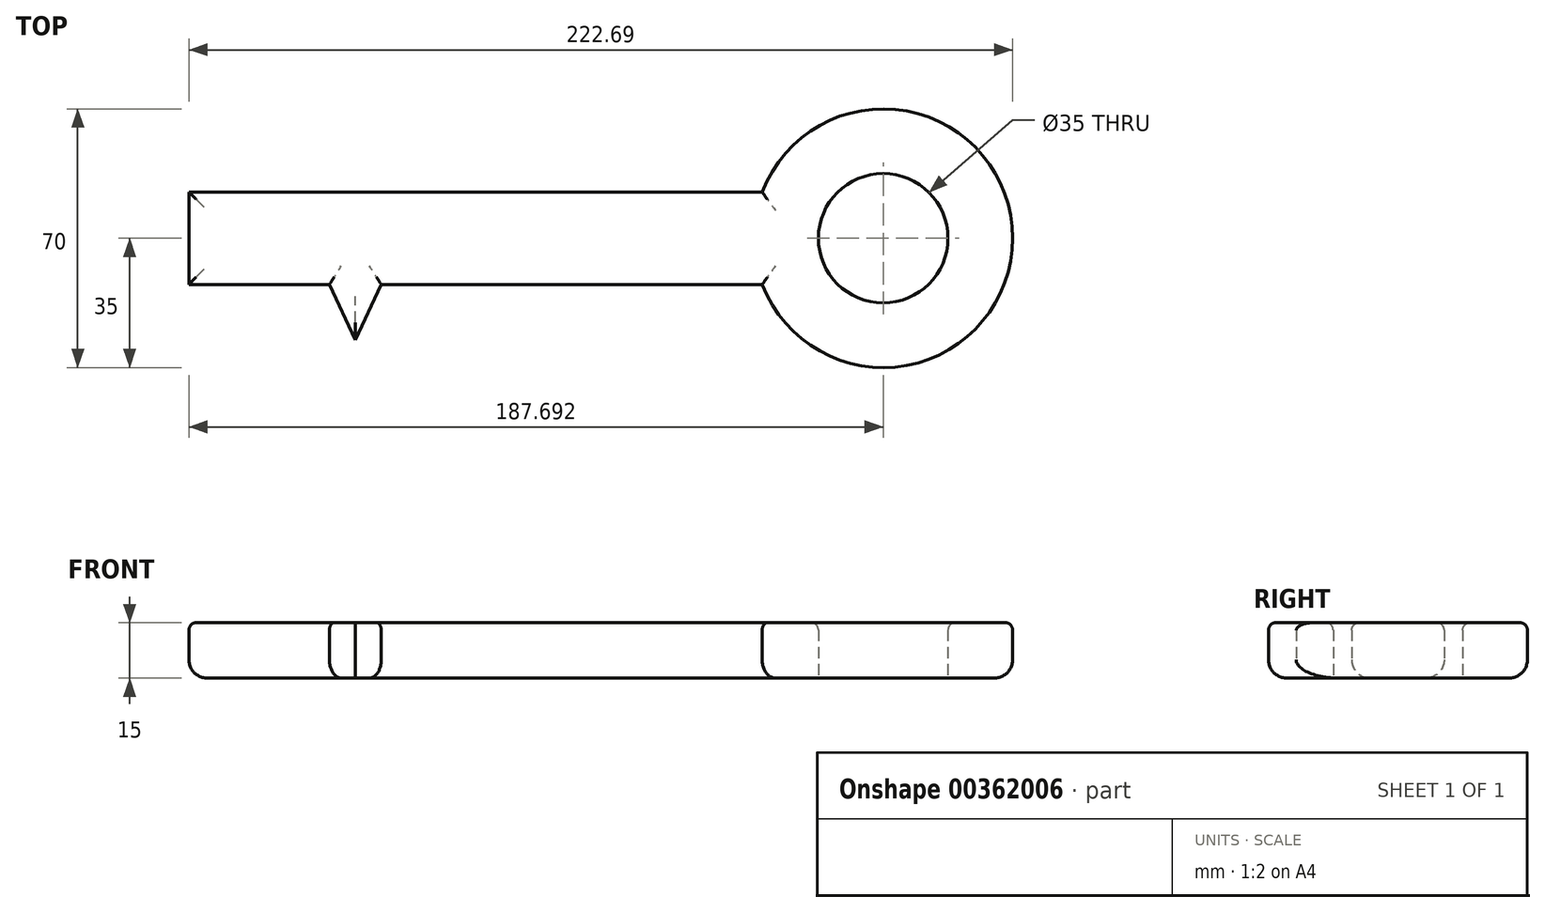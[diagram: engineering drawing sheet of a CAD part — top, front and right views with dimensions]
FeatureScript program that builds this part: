
annotation { "Feature Type Name" : "Feature", "Feature Type Description" : "" }
export const myFeature = defineFeature(function(context is Context, id is Id, definition is map)
    precondition{}
    {
        {
            var Q0;
            Q0=qCreatedBy(makeId("Top.planeOp"),FACE);
            var sketch = newSketch(context, id + "F0", { "sketchPlane" : qUnion([Q0])});
            skLineSegment(sketch, "E0.bottom", {"start": v(-155, 12.5) * mm, "end": v(0, 12.5) * mm});
            skLineSegment(sketch, "E0.top", {"start": v(-155, -12.5) * mm, "end": v(0, -12.5) * mm});
            skLineSegment(sketch, "E0.left", {"start": v(-155, 12.5) * mm, "end": v(-155, -12.5) * mm});
            skLineSegment(sketch, "E0.right", {"start": v(0, 12.5) * mm, "end": v(0, -12.5) * mm});
            skLineSegment(sketch, "E1.bottom", {"start": v(0, -12.5) * mm, "end": v(-155, -12.5) * mm});
            skLineSegment(sketch, "E1.top", {"start": v(0, -12.5) * mm, "end": v(-155, -12.5) * mm});
            skLineSegment(sketch, "E1.left", {"start": v(0, -12.5) * mm, "end": v(0, -12.5) * mm});
            skLineSegment(sketch, "E1.right", {"start": v(-155, -12.5) * mm, "end": v(-155, -12.5) * mm});
            skLineSegment(sketch, "E2.bottom", {"start": v(-155, -12.5) * mm, "end": v(-145, -12.5) * mm});
            skLineSegment(sketch, "E2.top", {"start": v(-155, -42.5) * mm, "end": v(-145, -42.5) * mm});
            skLineSegment(sketch, "E2.left", {"start": v(-155, -12.5) * mm, "end": v(-155, -42.5) * mm});
            skLineSegment(sketch, "E2.right", {"start": v(-145, -12.5) * mm, "end": v(-145, -42.5) * mm});
            skLineSegment(sketch, "E3.bottom", {"start": v(-135, -12.5) * mm, "end": v(-127, -12.5) * mm});
            skLineSegment(sketch, "E3.top", {"start": v(-135, -27.5) * mm, "end": v(-127, -27.5) * mm});
            skLineSegment(sketch, "E3.left", {"start": v(-135, -12.5) * mm, "end": v(-135, -27.5) * mm});
            skLineSegment(sketch, "E3.right", {"start": v(-127, -12.5) * mm, "end": v(-127, -27.5) * mm});
            skLineSegment(sketch, "E4", {"start": v(-117, -12.5) * mm, "end": v(-110, -27.5) * mm});
            skLineSegment(sketch, "E5", {"start": v(-110, -27.5) * mm, "end": v(-103, -12.5) * mm});
            skCircle(sketch, "E6", {"center": v(32.7, 0) * mm, "radius": 17.5 * mm});
            skArc(sketch, "E7", {"start": v(0, -12.5) * mm, "mid": v(67.7, 0) * mm, "end": v(0, 12.5) * mm});
            skSolve(sketch);
        }
        {
            var Q0;
            Q0=makeQuery(id+"F0.imprint","IMPRINT",FACE,{"disambiguationData":[TD([[makeQuery(id+"F0.imprint","IMPRINT",EDGE,{"derivedFrom":sQuery(id+"F0.wireOp",EDGE,"E2.bottom")}),-1.0]])]});
            var Q1;
            Q1=makeQuery(id+"F0.imprint","IMPRINT",FACE,{"disambiguationData":[TD([[makeQuery(id+"F0.imprint","IMPRINT",EDGE,{"derivedFrom":sQuery(id+"F0.wireOp",EDGE,"E3.bottom")}),-1.0]])]});
            var Q2;
            {var subQ0=sQuery(id+"F0.wireOp",EDGE,"E4");Q2=makeQuery(id+"F0.imprint","IMPRINT",FACE,{"disambiguationData":[TD([[makeQuery(id+"F0.imprint","IMPRINT",EDGE,{"derivedFrom":subQ0}),1.0]])]});}
            var Q3;
            Q3=makeQuery(id+"F0.imprint","IMPRINT",FACE,{"disambiguationData":[TD([[makeQuery(id+"F0.imprint","IMPRINT",EDGE,{"derivedFrom":sQuery(id+"F0.wireOp",EDGE,"E0.bottom")}),-1.0]])]});
            var Q4;
            Q4=makeQuery(id+"F0.imprint","IMPRINT",FACE,{"disambiguationData":[TD([[makeQuery(id+"F0.imprint","IMPRINT",EDGE,{"derivedFrom":sQuery(id+"F0.wireOp",EDGE,"E0.right")}),1.0]])]});
            extrude(context, id + "F1", {"entities" : qUnion([Q0, Q1, Q2, Q3, Q4]), "depth" : 15 * mm});
        }
        {
            var Q0;
            Q0=makeQuery(id+"F1.opExtrude","CAP_EDGE",EDGE,{"disambiguationData":[OSD([sQuery(id+"F0.wireOp",EDGE,"E7")])],"isStart":false});
            var Q1;
            Q1=makeQuery(id+"F1.opExtrude","CAP_EDGE",EDGE,{"disambiguationData":[OSD([sQuery(id+"F0.wireOp",EDGE,"E6")])],"isStart":false});
            var Q2;
            {var subQ0=sQuery(id+"F0.wireOp",EDGE,"E0.top");Q2=makeQuery(id+"F1.opExtrude","CAP_EDGE",EDGE,{"disambiguationData":[OSD([subQ0]),TDD([makeQuery(id+"F0.imprint","IMPRINT",EDGE,{"disambiguationData":[TD([[makeQuery(id+"F0.imprint","INTERSECT",VERTEX,{"derivedFrom":[subQ0,sQuery(id+"F0.wireOp",EDGE,"E5")]}),-1.0]])],"derivedFrom":subQ0})])],"isStart":false});}
            var Q3;
            Q3=makeQuery(id+"F1.opExtrude","CAP_EDGE",EDGE,{"disambiguationData":[OSD([sQuery(id+"F0.wireOp",EDGE,"E0.bottom")])],"isStart":false});
            var Q4;
            Q4=makeQuery(id+"F1.opExtrude","CAP_EDGE",EDGE,{"disambiguationData":[OSD([sQuery(id+"F0.wireOp",EDGE,"E5")])],"isStart":false});
            var Q5;
            Q5=makeQuery(id+"F1.opExtrude","CAP_EDGE",EDGE,{"disambiguationData":[OSD([sQuery(id+"F0.wireOp",EDGE,"E4")])],"isStart":false});
            var Q6;
            Q6=makeQuery(id+"F1.opExtrude","CAP_EDGE",EDGE,{"disambiguationData":[OSD([sQuery(id+"F0.wireOp",EDGE,"E3.top")])],"isStart":false});
            var Q7;
            Q7=makeQuery(id+"F1.opExtrude","CAP_FACE",FACE,{"disambiguationData":[OSD([sQuery(id+"F0.wireOp",EDGE,"E0.bottom"),sQuery(id+"F0.wireOp",EDGE,"E0.left"),sQuery(id+"F0.wireOp",EDGE,"E0.top"),sQuery(id+"F0.wireOp",EDGE,"E2.top"),sQuery(id+"F0.wireOp",EDGE,"E2.left"),sQuery(id+"F0.wireOp",EDGE,"E2.right"),sQuery(id+"F0.wireOp",EDGE,"E3.top"),sQuery(id+"F0.wireOp",EDGE,"E3.left"),sQuery(id+"F0.wireOp",EDGE,"E3.right"),sQuery(id+"F0.wireOp",EDGE,"E4"),sQuery(id+"F0.wireOp",EDGE,"E5"),sQuery(id+"F0.wireOp",EDGE,"E6"),sQuery(id+"F0.wireOp",EDGE,"E7")])],"isStart":false});
            fillet(context, id + "F2", {"entities" : qUnion([Q0, Q1, Q2, Q3, Q4, Q5, Q6, Q7]), "radius" : 2 * mm, "tangentPropagation" : true, "allowEdgeOverflow" : false});
        }
        {
            var Q0;
            Q0=makeQuery(id+"F1.opExtrude","CAP_EDGE",EDGE,{"disambiguationData":[OSD([sQuery(id+"F0.wireOp",EDGE,"E2.top")])],"isStart":true});
            var Q1;
            Q1=makeQuery(id+"F1.opExtrude","CAP_EDGE",EDGE,{"disambiguationData":[OSD([sQuery(id+"F0.wireOp",EDGE,"E2.right")])],"isStart":true});
            var Q2;
            Q2=makeQuery(id+"F1.opExtrude","CAP_EDGE",EDGE,{"disambiguationData":[OSD([sQuery(id+"F0.wireOp",EDGE,"E0.left"),sQuery(id+"F0.wireOp",EDGE,"E2.left")])],"isStart":true});
            var Q3;
            Q3=makeQuery(id+"F1.opExtrude","CAP_EDGE",EDGE,{"disambiguationData":[OSD([sQuery(id+"F0.wireOp",EDGE,"E0.bottom")])],"isStart":true});
            var Q4;
            Q4=makeQuery(id+"F1.opExtrude","CAP_EDGE",EDGE,{"disambiguationData":[OSD([sQuery(id+"F0.wireOp",EDGE,"E3.right")])],"isStart":true});
            var Q5;
            Q5=makeQuery(id+"F1.opExtrude","CAP_EDGE",EDGE,{"disambiguationData":[OSD([sQuery(id+"F0.wireOp",EDGE,"E3.left")])],"isStart":true});
            var Q6;
            {var subQ0=sQuery(id+"F0.wireOp",EDGE,"E0.top");Q6=makeQuery(id+"F1.opExtrude","CAP_EDGE",EDGE,{"disambiguationData":[OSD([subQ0]),TDD([makeQuery(id+"F0.imprint","IMPRINT",EDGE,{"disambiguationData":[TD([[makeQuery(id+"F0.imprint","INTERSECT",VERTEX,{"derivedFrom":[subQ0,sQuery(id+"F0.wireOp",EDGE,"E2.bottom"),sQuery(id+"F0.wireOp",EDGE,"E2.right")]}),-1.0]])],"derivedFrom":subQ0})])],"isStart":true});}
            var Q7;
            {var subQ0=sQuery(id+"F0.wireOp",EDGE,"E0.top");Q7=makeQuery(id+"F1.opExtrude","CAP_EDGE",EDGE,{"disambiguationData":[OSD([subQ0]),TDD([makeQuery(id+"F0.imprint","IMPRINT",EDGE,{"disambiguationData":[TD([[makeQuery(id+"F0.imprint","INTERSECT",VERTEX,{"derivedFrom":[subQ0,sQuery(id+"F0.wireOp",EDGE,"E4")]}),1.0]])],"derivedFrom":subQ0})])],"isStart":true});}
            var Q8;
            Q8=makeQuery(id+"F1.opExtrude","CAP_EDGE",EDGE,{"disambiguationData":[OSD([sQuery(id+"F0.wireOp",EDGE,"E4")])],"isStart":true});
            var Q9;
            Q9=makeQuery(id+"F1.opExtrude","CAP_EDGE",EDGE,{"disambiguationData":[OSD([sQuery(id+"F0.wireOp",EDGE,"E5")])],"isStart":true});
            var Q10;
            {var subQ0=sQuery(id+"F0.wireOp",EDGE,"E0.top");Q10=makeQuery(id+"F1.opExtrude","CAP_EDGE",EDGE,{"disambiguationData":[OSD([subQ0]),TDD([makeQuery(id+"F0.imprint","IMPRINT",EDGE,{"disambiguationData":[TD([[makeQuery(id+"F0.imprint","INTERSECT",VERTEX,{"derivedFrom":[subQ0,sQuery(id+"F0.wireOp",EDGE,"E5")]}),-1.0]])],"derivedFrom":subQ0})])],"isStart":true});}
            var Q11;
            Q11=makeQuery(id+"F1.opExtrude","CAP_EDGE",EDGE,{"disambiguationData":[OSD([sQuery(id+"F0.wireOp",EDGE,"E7")])],"isStart":true});
            fillet(context, id + "F3", {"entities" : qUnion([Q0, Q1, Q2, Q3, Q4, Q5, Q6, Q7, Q8, Q9, Q10, Q11]), "radius" : 5 * mm, "tangentPropagation" : true, "allowEdgeOverflow" : false});
        }
    });
